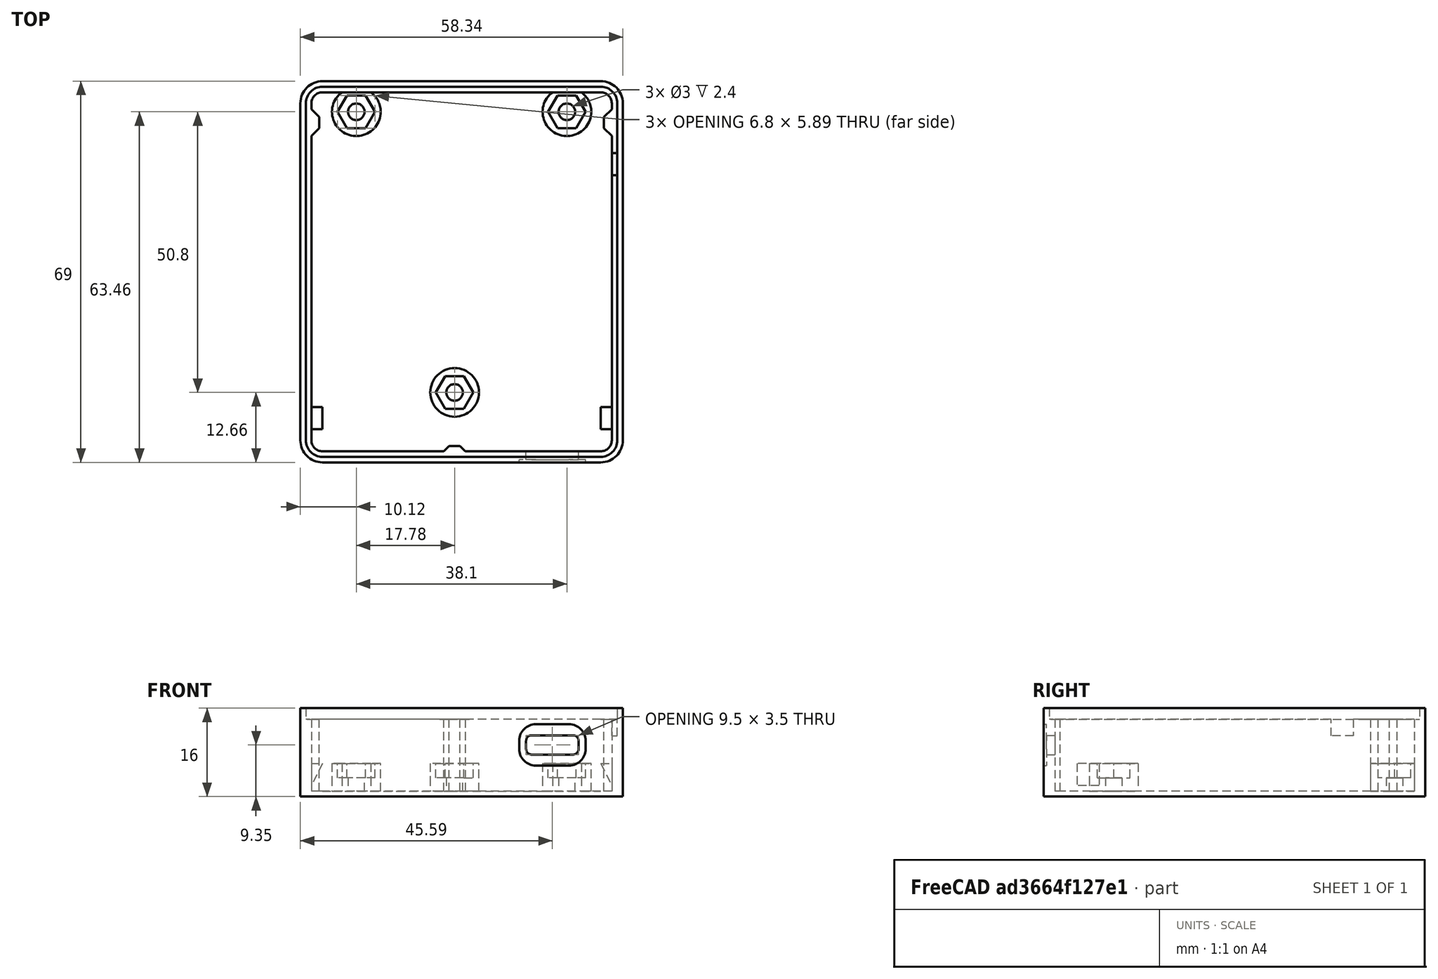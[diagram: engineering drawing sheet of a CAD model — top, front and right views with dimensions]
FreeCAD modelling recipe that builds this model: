
FCSTD DOCUMENT  (FreeCAD 0.18R15417 (Git))
Label: bneckfdmpla
License: CreativeCommons Attribution-ShareAlike
LicenseURL: http://creativecommons.org/licenses/by-sa/4.0/
objects: Sketcher::SketchObject×13, PartDesign::Pocket×6, PartDesign::Pad×5, Mesh::Feature×3, PartDesign::Fillet×3, TechDraw::DrawViewPart×3, Spreadsheet::Sheet×1, TechDraw::DrawSVGTemplate×1, PartDesign::Body×1, App::Part×1, TechDraw::DrawPage×1
note: 39 computed .brp shape members not serialized (recipe doc carries the construction recipe); baked Part::Feature solids carry a one-line shape summary decoded from their .brp

FEATURE [Sketcher::SketchObject] Sketch  label="Outline"
  MapMode = 5
  Support = -> [XY_Plane001]
  sketch-geometry (4):
    g0: LineSegment StartX=-26.67 StartY=32 StartZ=0 EndX=26.67 EndY=32 EndZ=0
    g1: LineSegment StartX=26.67 StartY=32 StartZ=0 EndX=26.67 EndY=-32 EndZ=0
    g2: LineSegment StartX=26.67 StartY=-32 StartZ=0 EndX=-26.67 EndY=-32 EndZ=0
    g3: LineSegment StartX=-26.67 StartY=-32 StartZ=0 EndX=-26.67 EndY=32 EndZ=0
  constraints (10):
    c: Coincident(g0,g1)
    c: Coincident(g1,g2)
    c: Coincident(g2,g3)
    c: Coincident(g3,g0)
    c: Horizontal(g2)
    c: Vertical(g1)
    c: DistanceY(g3,g3) = 64  'Length'
    c: DistanceX(g0,g0) = 53.34  'Width'
    c: Symmetric(g0,g0,g-2)
    c: Symmetric(g0,g2,g-1)
FEATURE [Spreadsheet::Sheet] Spreadsheet
  cells = A1=Nozzle Size; B1(nozzlesize)==0.40000000000000002mm; A2=Wall Thick; B2(wallthick)==nozzlesize * 5; A3=Wall Thin; B3(wallthin)==1mm; A4=Case Length; B4(caselength)==64mm; A5=Case Width; B5(casewidth)==53.340000000000003mm; A6=Case Height; B6(caseheight)==batthick + pcbthick + plateclear + platethick; A7=Batt Thick; B7(batthick)==6mm; A8=Nut Thick; B8(nutthick)==3.6000000000000001mm; A9=Nut Rad; B9(nutrad)==3.3999999999999999mm; A10=Plate Clear; B10(plateclear)==6.4000000000000004mm; A11=Plate Thick; B11(platethick)==2mm; A12=PCB Thick; B12(pcbthick)==1.6000000000000001mm; A13=PCB Offset; B13(pcboffset)==0.5mm
FEATURE [Sketcher::SketchObject] Sketch001  label="Outbox"
  ExternalGeometry = -> [Sketch]
  MapMode = 5
  Support = -> [XY_Plane001]
  expr: Constraints[7] = Spreadsheet.wallthick + Spreadsheet.pcboffset
  expr: Constraints[6] = Spreadsheet.wallthick + Spreadsheet.pcboffset
  sketch-geometry (4):
    g0: LineSegment StartX=-29.17 StartY=34.5 StartZ=0 EndX=29.17 EndY=34.5 EndZ=0
    g1: LineSegment StartX=29.17 StartY=34.5 StartZ=0 EndX=29.17 EndY=-34.5 EndZ=0
    g2: LineSegment StartX=29.17 StartY=-34.5 StartZ=0 EndX=-29.17 EndY=-34.5 EndZ=0
    g3: LineSegment StartX=-29.17 StartY=-34.5 StartZ=0 EndX=-29.17 EndY=34.5 EndZ=0
  constraints (10):
    c: Coincident(g0,g1)
    c: Coincident(g1,g2)
    c: Coincident(g2,g3)
    c: Coincident(g3,g0)
    c: Horizontal(g2)
    c: Vertical(g1)
    c: DistanceX(g0,g-3) = 2.5
    c: DistanceY(g-3,g0) = 2.5
    c: Symmetric(g0,g0,g-2)
    c: Symmetric(g0,g2,g-1)
FEATURE [PartDesign::Pad] Pad  label="Padmain"
  Length = 16
  Length2 = 100
  Profile = -> Sketch001
  Type = 0
  expr: Length = Spreadsheet.caseheight
FEATURE [Sketcher::SketchObject] Sketch002
  ExternalGeometry = -> [Sketch]
  MapMode = 5
  Placement = pos=(0,0,16) rot=(0,0,1;0rad)
  Support = -> [Pad]
  expr: Constraints[9] = Spreadsheet.pcboffset
  expr: Constraints[7] = Spreadsheet.pcboffset
  sketch-geometry (4):
    g0: LineSegment StartX=-27.17 StartY=32.5 StartZ=0 EndX=27.17 EndY=32.5 EndZ=0
    g1: LineSegment StartX=27.17 StartY=32.5 StartZ=0 EndX=27.17 EndY=-32.5 EndZ=0
    g2: LineSegment StartX=27.17 StartY=-32.5 StartZ=0 EndX=-27.17 EndY=-32.5 EndZ=0
    g3: LineSegment StartX=-27.17 StartY=-32.5 StartZ=0 EndX=-27.17 EndY=32.5 EndZ=0
  constraints (10):
    c: Coincident(g0,g1)
    c: Coincident(g1,g2)
    c: Coincident(g2,g3)
    c: Coincident(g3,g0)
    c: Horizontal(g2)
    c: Vertical(g1)
    c: Symmetric(g0,g0,g-2)
    c: DistanceY(g-3,g0) = 0.5
    c: Symmetric(g0,g2,g-1)
    c: DistanceX(g0,g-3) = 0.5
FEATURE [PartDesign::Pocket] Pocket  label="Pocketwallout"
  BaseFeature = -> Pad
  Length = 15
  Length2 = 100
  Profile = -> Sketch002
  Type = 0
  expr: Length = Padmain.Length - Spreadsheet.wallthin
FEATURE [Sketcher::SketchObject] Sketch003
  ExternalGeometry = -> [Sketch]
  MapMode = 5
  Placement = pos=(0,0,16) rot=(0,0,1;0rad)
  Support = -> [Pocket]
  expr: Constraints[9] = Spreadsheet.wallthick / 2 + Spreadsheet.pcboffset
  expr: Constraints[7] = Spreadsheet.wallthick / 2 + Spreadsheet.pcboffset
  sketch-geometry (4):
    g0: LineSegment StartX=-28.17 StartY=33.5 StartZ=0 EndX=28.17 EndY=33.5 EndZ=0
    g1: LineSegment StartX=28.17 StartY=33.5 StartZ=0 EndX=28.17 EndY=-33.5 EndZ=0
    g2: LineSegment StartX=28.17 StartY=-33.5 StartZ=0 EndX=-28.17 EndY=-33.5 EndZ=0
    g3: LineSegment StartX=-28.17 StartY=-33.5 StartZ=0 EndX=-28.17 EndY=33.5 EndZ=0
  constraints (10):
    c: Coincident(g0,g1)
    c: Coincident(g1,g2)
    c: Coincident(g2,g3)
    c: Coincident(g3,g0)
    c: Horizontal(g2)
    c: Vertical(g1)
    c: Symmetric(g0,g0,g-2)
    c: DistanceY(g-3,g0) = 1.5
    c: Symmetric(g0,g2,g-1)
    c: DistanceX(g0,g-3) = 1.5
FEATURE [PartDesign::Pocket] Pocket001  label="Pocketwallin"
  BaseFeature = -> Pocket
  Length = 2
  Length2 = 100
  Profile = -> Sketch003
  Type = 0
  expr: Length = Spreadsheet.platethick
FEATURE [Sketcher::SketchObject] Sketch004
  MapMode = 5
  Placement = pos=(0,0,1) rot=(0,0,1;0rad)
  Support = -> [Pocket001]
  sketch-geometry (6):
    g0: Circle CenterX=-19.05 CenterY=28.96 CenterZ=0 NormalX=0 NormalY=0 NormalZ=1 AngleXU=0 Radius=4.4
    g1: Circle CenterX=19.05 CenterY=28.96 CenterZ=0 NormalX=0 NormalY=0 NormalZ=1 AngleXU=0 Radius=4.4
    g2: Circle CenterX=-1.27 CenterY=-21.84 CenterZ=0 NormalX=0 NormalY=0 NormalZ=1 AngleXU=0 Radius=4.4
    g3: Circle CenterX=-19.05 CenterY=28.96 CenterZ=0 NormalX=0 NormalY=0 NormalZ=1 AngleXU=0 Radius=1.5
    g4: Circle CenterX=19.05 CenterY=28.96 CenterZ=0 NormalX=0 NormalY=0 NormalZ=1 AngleXU=0 Radius=1.5
    g5: Circle CenterX=-1.27 CenterY=-21.84 CenterZ=0 NormalX=0 NormalY=0 NormalZ=1 AngleXU=0 Radius=1.5
  constraints (9):
    c: Radius(g0) = 4.4  'Radouter-M3'
    c: Equal(g0,g1)
    c: Equal(g0,g2)
    c: Radius(g3) = 1.5
    c: Equal(g3,g4)
    c: Equal(g3,g5)
    c: Coincident(g0,g3)
    c: Coincident(g1,g4)
    c: Coincident(g2,g5)
FEATURE [TechDraw::DrawSVGTemplate] Template
  EditableTexts = Designed_by_Name=Monero Hardware; Drawing_number=1; FC-Date=December 2018; FC-SC=Scale; FC-SH=1; FC-Title=Breakneck Enclosure; Subtitle=Hardware wallet developer edition; Weight=Weight
  Height = 210
  Orientation = 1
  Width = 297
FEATURE [Sketcher::SketchObject] Sketch005
  ExternalGeometry = -> [Sketch]
  MapMode = 5
  Placement = pos=(0,-35,0) rot=(1,0,0;1.5708rad)
  expr: Constraints[18] = Spreadsheet.batthick + Spreadsheet.pcbthick
  sketch-geometry (8):
    g0: LineSegment StartX=12.67 StartY=11.1 StartZ=0 EndX=20.17 EndY=11.1 EndZ=0
    g1: LineSegment StartX=21.17 StartY=10.1 StartZ=0 EndX=21.17 EndY=8.6 EndZ=0
    g2: LineSegment StartX=20.17 StartY=7.6 StartZ=0 EndX=12.67 EndY=7.6 EndZ=0
    g3: LineSegment StartX=11.67 StartY=8.6 StartZ=0 EndX=11.67 EndY=10.1 EndZ=0
    g4: ArcOfCircle CenterX=12.67 CenterY=10.1 CenterZ=0 NormalX=0 NormalY=0 NormalZ=1 AngleXU=0 Radius=1 StartAngle=1.5708 EndAngle=3.14159
    g5: ArcOfCircle CenterX=12.67 CenterY=8.6 CenterZ=0 NormalX=0 NormalY=0 NormalZ=1 AngleXU=0 Radius=1 StartAngle=3.14159 EndAngle=4.71239
    g6: ArcOfCircle CenterX=20.17 CenterY=8.6 CenterZ=0 NormalX=0 NormalY=0 NormalZ=1 AngleXU=0 Radius=1 StartAngle=4.71239 EndAngle=6.28319
    g7: ArcOfCircle CenterX=20.17 CenterY=10.1 CenterZ=0 NormalX=0 NormalY=0 NormalZ=1 AngleXU=0 Radius=1 StartAngle=-9e-16 EndAngle=1.5708
  constraints (20):
    c: Horizontal(g0)
    c: Horizontal(g2)
    c: Vertical(g1)
    c: Vertical(g3)
    c: Tangent(g0,g4) = 1.5708
    c: Tangent(g3,g4) = 1.5708
    c: Tangent(g3,g5) = 1.5708
    c: Tangent(g2,g5) = 1.5708
    c: Tangent(g2,g6) = 1.5708
    c: Tangent(g1,g6) = 1.5708
    c: Tangent(g1,g7) = 1.5708
    c: Tangent(g0,g7) = 1.5708
    c: Radius(g4) = 1
    c: Equal(g4,g5)
    c: Equal(g4,g6)
    c: Equal(g4,g7)
    c: DistanceY(g2,g0) = 3.5
    c: DistanceX(g3,g1) = 9.5
    c: DistanceY(g-3,g2) = 7.6
    c: DistanceX(g1,g-3) = 5.5
FEATURE [PartDesign::Pocket] Pocket002  label="Pocketusbhole"
  BaseFeature = -> Pocket001
  Length = 3
  Length2 = 100
  Profile = -> Sketch005
  Type = 0
FEATURE [Sketcher::SketchObject] Sketch007
  AttachmentOffset = pos=(0,0,9.6) rot=(0,0,1;0rad)
  ExternalGeometry = -> [Sketch]
  MapMode = 5
  Placement = pos=(0,0,9.6) rot=(0,0,1;0rad)
  Support = -> [XY_Plane001]
  expr: AttachmentOffset.Base.z = Spreadsheet.caseheight - Spreadsheet.plateclear
  sketch-geometry (12):
    g0: LineSegment StartX=-27.97 StartY=30.2 StartZ=0 EndX=-25.77 EndY=28 EndZ=0
    g1: LineSegment StartX=-25.77 StartY=28 StartZ=0 EndX=-25.77 EndY=26 EndZ=0
    g2: LineSegment StartX=-25.77 StartY=26 StartZ=0 EndX=-27.97 EndY=23.8 EndZ=0
    g3: LineSegment StartX=-27.97 StartY=23.8 StartZ=0 EndX=-27.97 EndY=30.2 EndZ=0
    g4: LineSegment StartX=25.77 StartY=28 StartZ=0 EndX=25.77 EndY=26 EndZ=0
    g5: LineSegment StartX=25.77 StartY=26 StartZ=0 EndX=27.97 EndY=23.8 EndZ=0
    g6: LineSegment StartX=27.97 StartY=23.8 StartZ=0 EndX=27.97 EndY=30.2 EndZ=0
    g7: LineSegment StartX=27.97 StartY=30.2 StartZ=0 EndX=25.77 EndY=28 EndZ=0
    g8: LineSegment StartX=-2.27 StartY=-31.55 StartZ=0 EndX=-0.27 EndY=-31.55 EndZ=0
    g9: LineSegment StartX=-0.27 StartY=-31.55 StartZ=0 EndX=1.43 EndY=-33.25 EndZ=0
    g10: LineSegment StartX=1.43 StartY=-33.25 StartZ=0 EndX=-3.97 EndY=-33.25 EndZ=0
    g11: LineSegment StartX=-3.97 StartY=-33.25 StartZ=0 EndX=-2.27 EndY=-31.55 EndZ=0
  constraints (36):
    c: Coincident(g0,g1)
    c: Vertical(g1)
    c: Coincident(g1,g2)
    c: Coincident(g2,g3)
    c: Coincident(g3,g0)
    c: DistanceY(g1,g0) = 2
    c: Angle(g0,g1) = 2.35619
    c: Angle(g1,g2) = 2.35619
    c: Vertical(g3)
    c: DistanceX(g0,g0) = 2.2
    c: Coincident(g4,g5)
    c: Coincident(g5,g6)
    c: Coincident(g6,g7)
    c: Coincident(g7,g4)
    c: DistanceY(g4,g4) = 2
    c: Vertical(g4)
    c: Angle(g4,g7) = 2.35619
    c: Angle(g5,g4) = 2.35619
    c: Vertical(g6)
    c: DistanceX(g4,g6) = 2.2
    c: Coincident(g8,g9)
    c: Coincident(g9,g10)
    c: Coincident(g10,g11)
    c: Coincident(g11,g8)
    c: Horizontal(g10)
    c: Angle(g11,g8) = 2.35619
    c: Angle(g8,g9) = 2.35619
    c: DistanceX(g8,g8) = 2
    c: DistanceY(g9,g8) = 1.7
    c: DistanceY(g0,g-3) = 4
    c: DistanceX(g-3,g0) = 0.9
    c: DistanceY(g4,g-3) = 4
    c: DistanceX(g4,g-3) = 0.9
    c: DistanceY(g-4,g8) = 0.45
    c: Horizontal(g8)
    c: DistanceX(g-4,g8) = 24.4
FEATURE [PartDesign::Pad] Pad003  label="Padshienen"
  BaseFeature = -> Pocket002
  Length = 4.4
  Length2 = 9
  Offset = 8
  Profile = -> Sketch007
  Type = 4
  expr: Length2 = Spreadsheet.plateclear + Spreadsheet.wallthin + Spreadsheet.pcbthick
  expr: Length = Spreadsheet.plateclear - Spreadsheet.platethick
FEATURE [Sketcher::SketchObject] Sketch008
  ExternalGeometry = -> [Sketch]
  MapMode = 5
  Support = -> [XY_Plane001]
  expr: Constraints[54] = Spreadsheet.nutrad
  expr: Constraints[53] = Spreadsheet.nutrad
  expr: Constraints[18] = Spreadsheet.nutrad
  sketch-geometry (24):
    g0: LineSegment StartX=0.43 StartY=-24.7845 StartZ=0 EndX=2.13 EndY=-21.84 EndZ=0
    g1: LineSegment StartX=2.13 StartY=-21.84 StartZ=0 EndX=0.43 EndY=-18.8955 EndZ=0
    g2: LineSegment StartX=0.43 StartY=-18.8955 StartZ=0 EndX=-2.97 EndY=-18.8955 EndZ=0
    g3: LineSegment StartX=-2.97 StartY=-18.8955 StartZ=0 EndX=-4.67 EndY=-21.84 EndZ=0
    g4: LineSegment StartX=-4.67 StartY=-21.84 StartZ=0 EndX=-2.97 EndY=-24.7845 EndZ=0
    g5: LineSegment StartX=-2.97 StartY=-24.7845 StartZ=0 EndX=0.43 EndY=-24.7845 EndZ=0
    g6: Circle [constr] CenterX=-1.27 CenterY=-21.84 CenterZ=0 NormalX=0 NormalY=0 NormalZ=1 AngleXU=0 Radius=3.4
    g7: LineSegment StartX=-15.65 StartY=28.96 StartZ=0 EndX=-17.35 EndY=31.9045 EndZ=0
    g8: LineSegment StartX=-17.35 StartY=31.9045 StartZ=0 EndX=-20.75 EndY=31.9045 EndZ=0
    g9: LineSegment StartX=-20.75 StartY=31.9045 StartZ=0 EndX=-22.45 EndY=28.96 EndZ=0
    g10: LineSegment StartX=-22.45 StartY=28.96 StartZ=0 EndX=-20.75 EndY=26.0155 EndZ=0
    g11: LineSegment StartX=-20.75 StartY=26.0155 StartZ=0 EndX=-17.35 EndY=26.0155 EndZ=0
    g12: LineSegment StartX=-17.35 StartY=26.0155 StartZ=0 EndX=-15.65 EndY=28.96 EndZ=0
    g13: Circle [constr] CenterX=-19.05 CenterY=28.96 CenterZ=0 NormalX=0 NormalY=0 NormalZ=1 AngleXU=0 Radius=3.4
    g14: LineSegment StartX=20.75 StartY=26.0155 StartZ=0 EndX=22.45 EndY=28.96 EndZ=0
    g15: LineSegment StartX=22.45 StartY=28.96 StartZ=0 EndX=20.75 EndY=31.9045 EndZ=0
    g16: LineSegment StartX=20.75 StartY=31.9045 StartZ=0 EndX=17.35 EndY=31.9045 EndZ=0
    g17: LineSegment StartX=17.35 StartY=31.9045 StartZ=0 EndX=15.65 EndY=28.96 EndZ=0
    g18: LineSegment StartX=15.65 StartY=28.96 StartZ=0 EndX=17.35 EndY=26.0155 EndZ=0
    g19: LineSegment StartX=17.35 StartY=26.0155 StartZ=0 EndX=20.75 EndY=26.0155 EndZ=0
    g20: Circle [constr] CenterX=19.05 CenterY=28.96 CenterZ=0 NormalX=0 NormalY=0 NormalZ=1 AngleXU=0 Radius=3.4
    g21: Circle CenterX=-19.05 CenterY=28.96 CenterZ=0 NormalX=0 NormalY=0 NormalZ=1 AngleXU=0 Radius=4.4
    g22: Circle CenterX=19.05 CenterY=28.96 CenterZ=0 NormalX=0 NormalY=0 NormalZ=1 AngleXU=0 Radius=4.4
    g23: Circle CenterX=-1.27 CenterY=-21.84 CenterZ=0 NormalX=0 NormalY=0 NormalZ=1 AngleXU=0 Radius=4.4
  constraints (56):
    c: Coincident(g0,g1)
    c: Coincident(g1,g2)
    c: Coincident(g2,g3)
    c: Coincident(g3,g4)
    c: Coincident(g4,g5)
    c: Coincident(g5,g0)
    c: Equal(g0, g1-g5) x5
    c: PointOnObject(g0,g6)
    c: PointOnObject(g1,g6)
    c: PointOnObject(g2,g6)
    c: PointOnObject(g3,g6)
    c: PointOnObject(g4,g6)
    c: PointOnObject(g5,g6)
    c: Horizontal(g5)
    c: Radius(g6) = 3.4
    c: Coincident(g7,g8)
    c: Coincident(g8,g9)
    c: Coincident(g9,g10)
    c: Coincident(g10,g11)
    c: Coincident(g11,g12)
    c: Coincident(g12,g7)
    c: Equal(g7, g8-g12) x5
    c: PointOnObject(g7,g13)
    c: PointOnObject(g8,g13)
    c: PointOnObject(g9,g13)
    c: PointOnObject(g10,g13)
    c: PointOnObject(g11,g13)
    c: PointOnObject(g12,g13)
    c: Coincident(g14,g15)
    c: Coincident(g15,g16)
    c: Coincident(g16,g17)
    c: Coincident(g17,g18)
    c: Coincident(g18,g19)
    c: Coincident(g19,g14)
    c: Equal(g14, g15-g19) x5
    c: PointOnObject(g14,g20)
    c: PointOnObject(g15,g20)
    c: PointOnObject(g16,g20)
    c: PointOnObject(g17,g20)
    c: PointOnObject(g18,g20)
    c: PointOnObject(g19,g20)
    c: Radius(g13) = 3.4
    c: Radius(g20) = 3.4
    c: DistanceY(g13,g-3) = 3.04
    c: DistanceX(g13,g20) = 38.1
    c: Horizontal(g11)
    c: Horizontal(g19)
    c: Symmetric(g13,g20,g-2)
    c: DistanceY(g6,g13) = 50.8
    c: DistanceX(g13,g6) = 17.78
    c: Radius(g21) = 4.4
    c: Equal(g21,g22)
    c: Equal(g21,g23)
    c: Coincident(g21,g13)
    c: Coincident(g22,g20)
    c: Coincident(g23,g6)
FEATURE [PartDesign::Pad] Pad004  label="Padmntbot"
  BaseFeature = -> Pad003
  Length = 2.4
  Length2 = 100
  Profile = -> Sketch004
  Type = 0
  expr: Length = Spreadsheet.batthick - Spreadsheet.nutthick
FEATURE [PartDesign::Pad] Pad005  label="Padmnttop"
  BaseFeature = -> Pad004
  Length = 6
  Length2 = 100
  Profile = -> Sketch008
  Type = 0
  expr: Length = Spreadsheet.batthick
FEATURE [Sketcher::SketchObject] Sketch009
  ExternalGeometry = -> [Sketch003]
  MapMode = 5
  Placement = pos=(0,0,0) rot=(0.57735,0.57735,0.57735;2.0944rad)
  Support = -> [YZ_Plane001]
  expr: Constraints[9] = Spreadsheet.platethick + 2mm
  expr: Constraints[11] = Spreadsheet.platethick - 1mm
  sketch-geometry (4):
    g0: LineSegment StartX=17.5 StartY=15 StartZ=0 EndX=21.5 EndY=15 EndZ=0
    g1: LineSegment StartX=21.5 StartY=15 StartZ=0 EndX=21.5 EndY=11 EndZ=0
    g2: LineSegment StartX=21.5 StartY=11 StartZ=0 EndX=17.5 EndY=11 EndZ=0
    g3: LineSegment StartX=17.5 StartY=11 StartZ=0 EndX=17.5 EndY=15 EndZ=0
  constraints (12):
    c: Coincident(g0,g1)
    c: Coincident(g1,g2)
    c: Coincident(g2,g3)
    c: Coincident(g3,g0)
    c: Horizontal(g0)
    c: Horizontal(g2)
    c: Vertical(g1)
    c: Vertical(g3)
    c: DistanceX(g0,g0) = 4
    c: DistanceY(g2,g0) = 4
    c: DistanceX(g0,g-3) = 12
    c: DistanceY(g0,g-3) = 1
FEATURE [PartDesign::Pocket] Pocket003  label="Pocketplatrem"
  BaseFeature = -> Pad005
  Length = 28.17
  Length2 = 100
  Profile = -> Sketch009
  Reversed = true
  Type = 0
  expr: Length = Spreadsheet.casewidth / 2 + Spreadsheet.pcboffset + Spreadsheet.wallthin
FEATURE [Sketcher::SketchObject] Sketch011
  ExternalGeometry = -> [Sketch]
  MapMode = 5
  Placement = pos=(0,-35,0) rot=(1,0,0;1.5708rad)
  expr: Constraints[18] = Spreadsheet.batthick + Spreadsheet.pcbthick - 2mm
  sketch-geometry (8):
    g0: LineSegment StartX=13.42 StartY=13.1 StartZ=0 EndX=19.42 EndY=13.1 EndZ=0
    g1: LineSegment StartX=22.42 StartY=10.1 StartZ=0 EndX=22.42 EndY=8.6 EndZ=0
    g2: LineSegment StartX=19.42 StartY=5.6 StartZ=0 EndX=13.42 EndY=5.6 EndZ=0
    g3: LineSegment StartX=10.42 StartY=8.6 StartZ=0 EndX=10.42 EndY=10.1 EndZ=0
    g4: ArcOfCircle CenterX=13.42 CenterY=10.1 CenterZ=0 NormalX=0 NormalY=0 NormalZ=1 AngleXU=0 Radius=3 StartAngle=1.5708 EndAngle=3.14159
    g5: ArcOfCircle CenterX=13.42 CenterY=8.6 CenterZ=0 NormalX=0 NormalY=0 NormalZ=1 AngleXU=0 Radius=3 StartAngle=3.14159 EndAngle=4.71239
    g6: ArcOfCircle CenterX=19.42 CenterY=8.6 CenterZ=0 NormalX=0 NormalY=0 NormalZ=1 AngleXU=0 Radius=3 StartAngle=4.71239 EndAngle=6.28319
    g7: ArcOfCircle CenterX=19.42 CenterY=10.1 CenterZ=0 NormalX=0 NormalY=0 NormalZ=1 AngleXU=0 Radius=3 StartAngle=0 EndAngle=1.5708
  constraints (20):
    c: Horizontal(g0)
    c: Horizontal(g2)
    c: Vertical(g1)
    c: Vertical(g3)
    c: Tangent(g0,g4) = 1.5708
    c: Tangent(g3,g4) = 1.5708
    c: Tangent(g3,g5) = 1.5708
    c: Tangent(g2,g5) = 1.5708
    c: Tangent(g2,g6) = 1.5708
    c: Tangent(g1,g6) = 1.5708
    c: Tangent(g1,g7) = 1.5708
    c: Tangent(g0,g7) = 1.5708
    c: Radius(g4) = 3
    c: Equal(g4,g5)
    c: Equal(g4,g6)
    c: Equal(g4,g7)
    c: DistanceY(g2,g0) = 7.5
    c: DistanceX(g3,g1) = 12
    c: DistanceY(g-3,g2) = 5.6
    c: DistanceX(g1,g-3) = 4.25
FEATURE [PartDesign::Pocket] Pocket004  label="Pocketplug"
  BaseFeature = -> Pocket003
  Length = 1
  Length2 = 100
  Profile = -> Sketch011
  Type = 0
FEATURE [Sketcher::SketchObject] Sketch013
  AttachmentOffset = pos=(0,0,1) rot=(0,0,1;0rad)
  ExternalGeometry = -> [Sketch007,Sketch002]
  MapMode = 5
  Placement = pos=(1,-2e-16,2e-16) rot=(0.57735,0.57735,0.57735;2.0944rad)
  Support = -> [YZ_Plane001]
  sketch-geometry (4):
    g0: LineSegment StartX=-30.5 StartY=13.6 StartZ=0 EndX=-32.5 EndY=9.6 EndZ=0
    g1: LineSegment StartX=-32.5 StartY=9.6 StartZ=0 EndX=-30.5 EndY=9.6 EndZ=0
    g2: LineSegment StartX=-30.5 StartY=9.6 StartZ=0 EndX=-30.5 EndY=13.6 EndZ=0
    g3: Circle [constr] CenterX=-31.5 CenterY=11.6 CenterZ=0 NormalX=0 NormalY=0 NormalZ=1 AngleXU=0 Radius=2.23607
  constraints (12):
    c: Coincident(g0,g1)
    c: Coincident(g1,g2)
    c: Coincident(g2,g0)
    c: PointOnObject(g0,g3)
    c: PointOnObject(g1,g3)
    c: PointOnObject(g2,g3)
    c: Horizontal(g1)
    c: Angle(g2,g1) = 1.5708
    c: DistanceX(g1,g1) = 2
    c: DistanceY(g2,g2) = 4
    c: PointOnObject(g-3,g1)
    c: Vertical(g-4,g0)
FEATURE [Mesh::Feature] Mesh  label="Meshbrims16"
FEATURE [Sketcher::SketchObject] Sketch014
  AttachmentOffset = pos=(0,0,6) rot=(0,0,1;0rad)
  ExternalGeometry = -> [Sketch002]
  MapMode = 5
  Placement = pos=(0,0,6) rot=(0,0,1;0rad)
  Support = -> [XY_Plane001]
  expr: AttachmentOffset.Base.z = Spreadsheet.batthick
  sketch-geometry (8):
    g0: LineSegment StartX=25.17 StartY=-24.5 StartZ=0 EndX=27.17 EndY=-24.5 EndZ=0
    g1: LineSegment StartX=27.17 StartY=-24.5 StartZ=0 EndX=27.17 EndY=-28.5 EndZ=0
    g2: LineSegment StartX=27.17 StartY=-28.5 StartZ=0 EndX=25.17 EndY=-28.5 EndZ=0
    g3: LineSegment StartX=25.17 StartY=-28.5 StartZ=0 EndX=25.17 EndY=-24.5 EndZ=0
    g4: LineSegment StartX=-27.17 StartY=-24.5 StartZ=0 EndX=-25.17 EndY=-24.5 EndZ=0
    g5: LineSegment StartX=-25.17 StartY=-24.5 StartZ=0 EndX=-25.17 EndY=-28.5 EndZ=0
    g6: LineSegment StartX=-25.17 StartY=-28.5 StartZ=0 EndX=-27.17 EndY=-28.5 EndZ=0
    g7: LineSegment StartX=-27.17 StartY=-28.5 StartZ=0 EndX=-27.17 EndY=-24.5 EndZ=0
  constraints (23):
    c: Coincident(g0,g1)
    c: Coincident(g1,g2)
    c: Coincident(g2,g3)
    c: Coincident(g3,g0)
    c: Horizontal(g0)
    c: Horizontal(g2)
    c: Vertical(g1)
    c: Vertical(g3)
    c: Coincident(g4,g5)
    c: Coincident(g5,g6)
    c: Coincident(g6,g7)
    c: Coincident(g7,g4)
    c: Horizontal(g4)
    c: Horizontal(g6)
    c: Vertical(g5)
    c: Vertical(g7)
    c: DistanceY(g3,g3) = 4
    c: DistanceX(g0,g0) = 2
    c: PointOnObject(g0,g-3)
    c: DistanceY(g-3,g1) = 4
    c: Equal(g1,g5)
    c: Equal(g0,g4)
    c: Symmetric(g5,g2,g-2)
FEATURE [PartDesign::Pad] Pad007  label="Padsideribs"
  BaseFeature = -> Pocket004
  Length = 4
  Length2 = 4
  Profile = -> Sketch014
  Reversed = true
  Type = 0
FEATURE [Sketcher::SketchObject] Sketch015
  AttachmentOffset = pos=(0,0,24) rot=(0,0,1;0rad)
  ExternalGeometry = -> [Sketch014]
  MapMode = 5
  Placement = pos=(0,-24,-5.3e-15) rot=(1,0,0;1.5708rad)
  Support = -> [XZ_Plane001]
  expr: AttachmentOffset.Base.z = Spreadsheet.caselength / 2 - 8mm
  sketch-geometry (8):
    g0: LineSegment StartX=27.17 StartY=2 StartZ=0 EndX=25.17 EndY=6 EndZ=0
    g1: LineSegment StartX=25.17 StartY=6 StartZ=0 EndX=25.17 EndY=2 EndZ=0
    g2: LineSegment StartX=25.17 StartY=2 StartZ=0 EndX=27.17 EndY=2 EndZ=0
    g3: Circle [constr] CenterX=26.17 CenterY=4 CenterZ=0 NormalX=0 NormalY=0 NormalZ=1 AngleXU=0 Radius=2.23607
    g4: LineSegment StartX=-25.17 StartY=2 StartZ=0 EndX=-25.17 EndY=6 EndZ=0
    g5: LineSegment StartX=-25.17 StartY=6 StartZ=0 EndX=-27.17 EndY=2 EndZ=0
    g6: LineSegment StartX=-27.17 StartY=2 StartZ=0 EndX=-25.17 EndY=2 EndZ=0
    g7: Circle [constr] CenterX=-26.17 CenterY=4 CenterZ=0 NormalX=0 NormalY=0 NormalZ=1 AngleXU=0 Radius=2.23607
  constraints (22):
    c: Coincident(g0,g1)
    c: Coincident(g1,g2)
    c: Coincident(g2,g0)
    c: PointOnObject(g0,g3)
    c: PointOnObject(g1,g3)
    c: PointOnObject(g2,g3)
    c: Angle(g2,g1) = 1.5708
    c: Horizontal(g2)
    c: DistanceY(g1,g1) = 4
    c: DistanceX(g2,g2) = 2
    c: Coincident(g0,g-3)
    c: Coincident(g4,g5)
    c: Coincident(g5,g6)
    c: Coincident(g6,g4)
    c: PointOnObject(g4,g7)
    c: PointOnObject(g5,g7)
    c: PointOnObject(g6,g7)
    c: Angle(g4,g6) = 1.5708
    c: Horizontal(g6)
    c: Equal(g4,g1)
    c: Equal(g6,g2)
    c: Symmetric(g1,g4,g-2)
FEATURE [PartDesign::Pocket] Pocket007
  BaseFeature = -> Pad007
  Length = 6
  Length2 = 100
  Profile = -> Sketch015
  Reversed = true
  Type = 0
FEATURE [Mesh::Feature] Mesh001  label="Meshsideribs"
FEATURE [PartDesign::Fillet] Fillet
  Base = -> Pocket007 [Edge127,Edge139,Edge142,Edge109]
  BaseFeature = -> Pocket007
  Radius = 2
FEATURE [PartDesign::Fillet] Fillet001
  Base = -> Fillet [Edge63,Edge65,Edge60,Edge56]
  BaseFeature = -> Fillet
  Radius = 3
FEATURE [PartDesign::Fillet] Fillet002
  Base = -> Fillet001 [Edge207,Edge204,Edge205,Edge209]
  BaseFeature = -> Fillet001
  Radius = 4
FEATURE [PartDesign::Body] Body
  Group = -> [Sketch,Sketch001,Pad,Sketch002,Pocket,Sketch003,Pocket001,Sketch004,Sketch005,Pocket002,Sketch007,Pad003,Sketch008,Pad004,Pad005,Sketch009,Pocket003,Sketch011,Pocket004,Sketch013,Sketch014,Pad007,Sketch015,Pocket007,Fillet,Fillet001,Fillet002]
  Origin = -> Origin001
  Tip = -> Fillet002
FEATURE [App::Part] Part
  Group = -> [Body]
  Origin = -> Origin
FEATURE [TechDraw::DrawViewPart] View001
  CoarseView = false
  Direction = (0,-1,0)
  Focus = 100
  HardHidden = false
  IsoCount = 0
  IsoHidden = false
  IsoVisible = false
  LockPosition = false
  Perspective = false
  Rotation = 0
  ScaleType = 0
  SeamHidden = false
  SeamVisible = false
  SmoothHidden = false
  SmoothVisible = false
  Source = -> [Part]
  X = 78.7998
  Y = 158.512
FEATURE [TechDraw::DrawViewPart] View002
  CoarseView = false
  Direction = (0.577,-0.577,0.577)
  Focus = 100
  HardHidden = false
  IsoCount = 0
  IsoHidden = false
  IsoVisible = false
  LockPosition = false
  Perspective = false
  Rotation = 0
  ScaleType = 0
  SeamHidden = false
  SeamVisible = false
  SmoothHidden = false
  SmoothVisible = false
  Source = -> [Part]
  X = 79.6991
  Y = 69.0257
FEATURE [TechDraw::DrawViewPart] View
  CoarseView = false
  Direction = (0,0,1)
  Focus = 100
  HardHidden = false
  IsoCount = 0
  IsoHidden = false
  IsoVisible = false
  LockPosition = false
  Perspective = false
  Rotation = 0
  ScaleType = 0
  SeamHidden = false
  SeamVisible = false
  SmoothHidden = false
  SmoothVisible = false
  Source = -> [Part]
  X = 211.005
  Y = 128.383
FEATURE [TechDraw::DrawPage] Page
  KeepUpdated = true
  ProjectionType = 0
  Template = -> Template
  Views = -> [View001,View002,View]
FEATURE [Mesh::Feature] Mesh002  label="Body (Meshed)"
